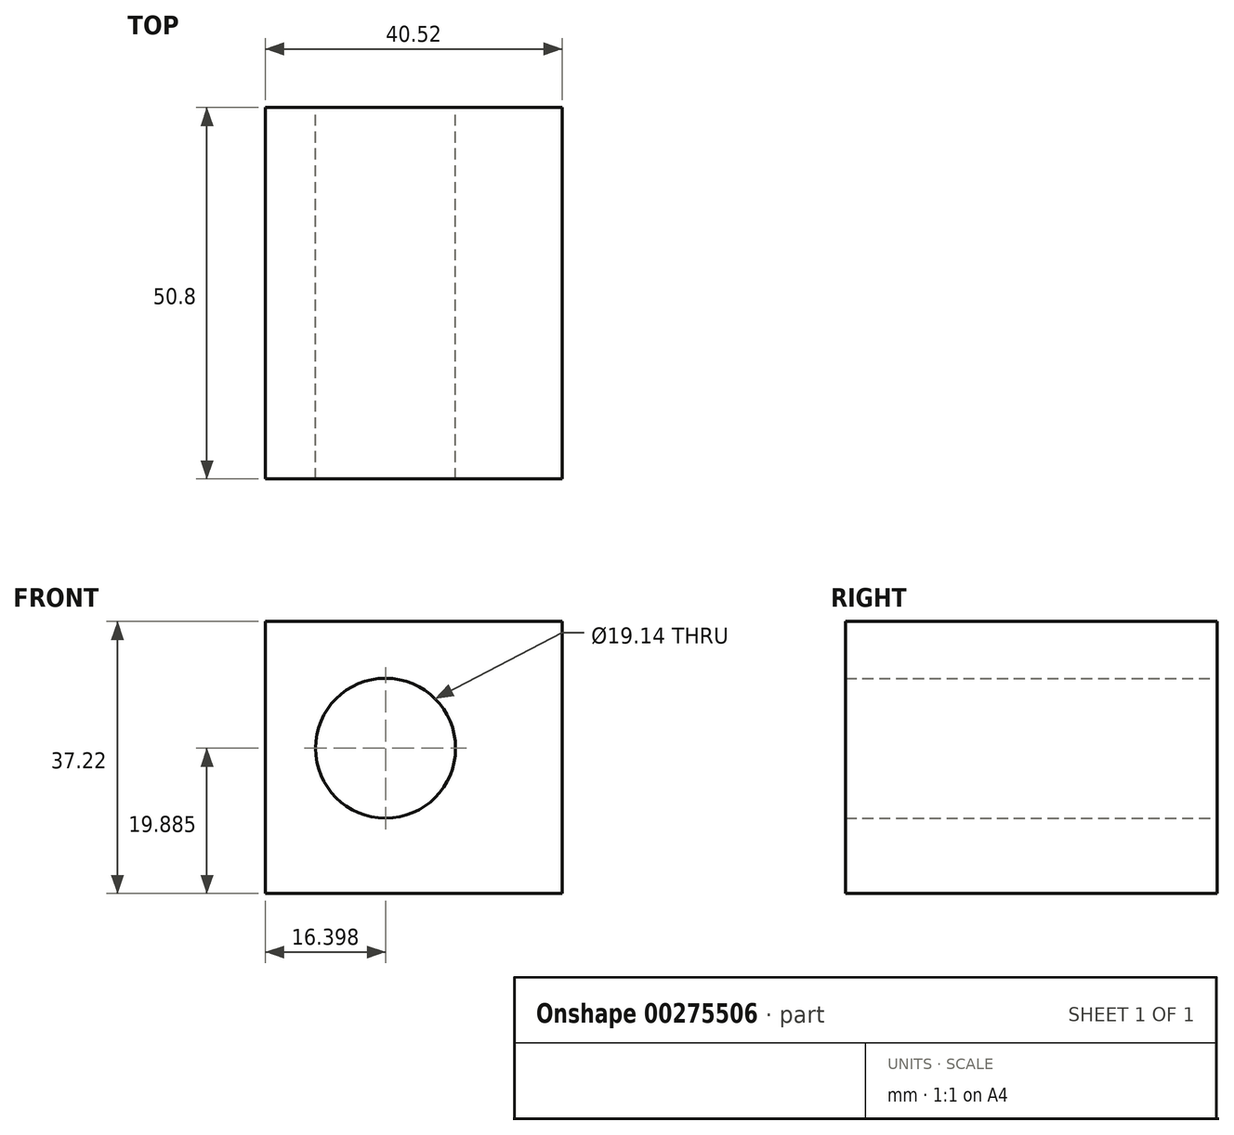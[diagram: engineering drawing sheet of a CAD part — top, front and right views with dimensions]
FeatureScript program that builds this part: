
annotation { "Feature Type Name" : "Feature", "Feature Type Description" : "" }
export const myFeature = defineFeature(function(context is Context, id is Id, definition is map)
    precondition{}
    {
        {
            var Q0;
            Q0=qCreatedBy(makeId("Front.planeOp"),FACE);
            var sketch = newSketch(context, id + "F0", { "sketchPlane" : qUnion([Q0])});
            skLineSegment(sketch, "E0.bottom", {"start": v(0, 0) * mm, "end": v(40.52, 0) * mm});
            skLineSegment(sketch, "E0.top", {"start": v(0, 37.22) * mm, "end": v(40.52, 37.22) * mm});
            skLineSegment(sketch, "E0.left", {"start": v(0, 0) * mm, "end": v(0, 37.22) * mm});
            skLineSegment(sketch, "E0.right", {"start": v(40.52, 0) * mm, "end": v(40.52, 37.22) * mm});
            skCircle(sketch, "E1", {"center": v(16.4, 19.88) * mm, "radius": 9.57 * mm});
            skSolve(sketch);
        }
        {
            var Q0;
            Q0=makeQuery(id+"F0.imprint","IMPRINT",FACE,{"disambiguationData":[TD([[makeQuery(id+"F0.imprint","IMPRINT",EDGE,{"derivedFrom":sQuery(id+"F0.wireOp",EDGE,"E0.bottom")}),1.0]])]});
            extrude(context, id + "F1", {"entities" : qUnion([Q0]), "depth" : 50.8 * mm});
        }
    });
